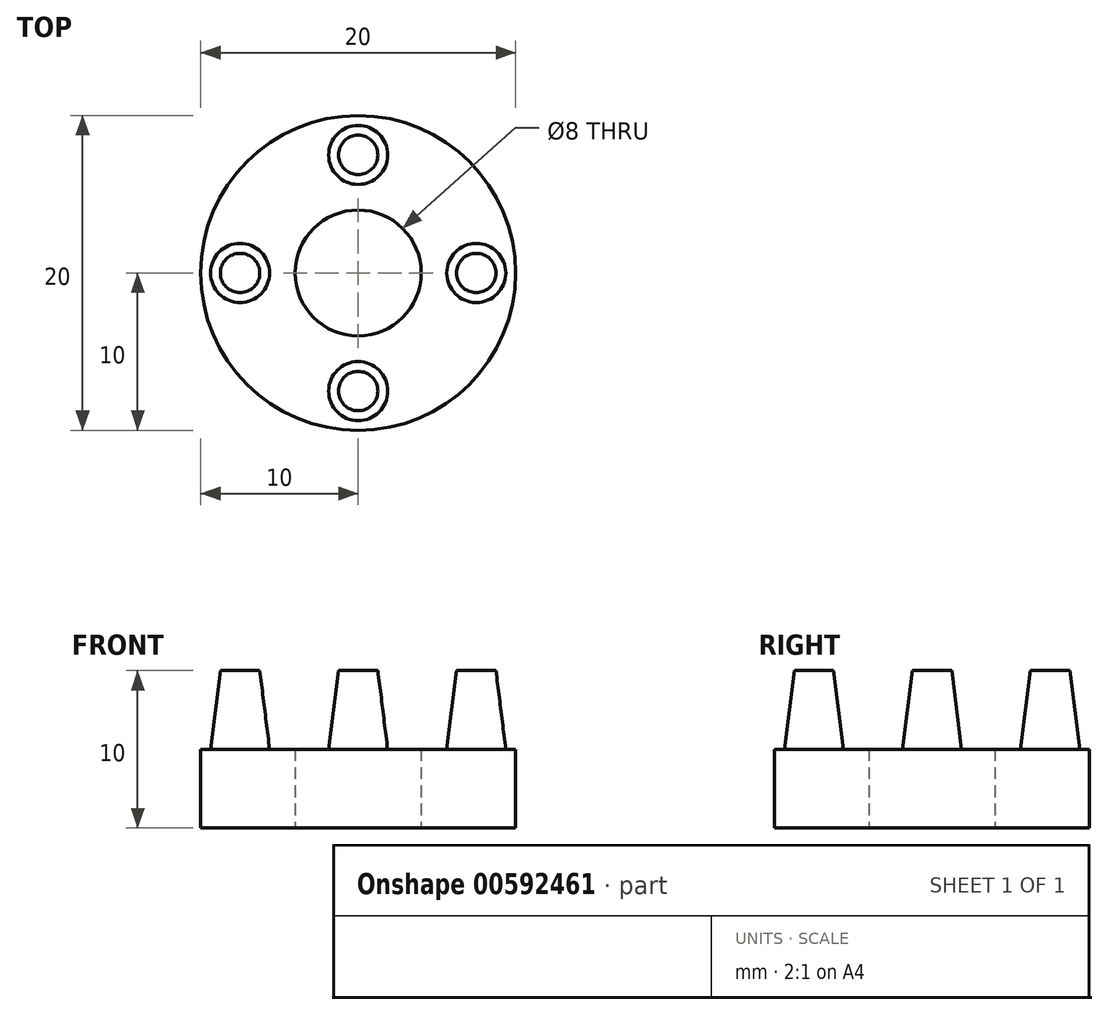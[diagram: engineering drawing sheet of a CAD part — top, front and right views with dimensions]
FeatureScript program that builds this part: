
annotation { "Feature Type Name" : "Feature", "Feature Type Description" : "" }
export const myFeature = defineFeature(function(context is Context, id is Id, definition is map)
    precondition{}
    {
        {
            var Q0;
            Q0=qCreatedBy(makeId("Top.planeOp"),FACE);
            var sketch = newSketch(context, id + "F0", { "sketchPlane" : qUnion([Q0])});
            skCircle(sketch, "E0", {"center": v(0, 0) * mm, "radius": 4 * mm});
            skCircle(sketch, "E1", {"center": v(0, 0) * mm, "radius": 10 * mm});
            skCircle(sketch, "E2", {"center": v(0, 7.5) * mm, "radius": 2.5 * mm});
            skSolve(sketch);
        }
        {
            var Q0;
            {var subQ1=sQuery(id+"F0.wireOp",EDGE,"E2");Q0=makeQuery(id+"F0.imprint","IMPRINT",FACE,{"disambiguationData":[TD([[makeQuery(id+"F0.imprint","IMPRINT",EDGE,{"derivedFrom":subQ1}),-1.0]])]});}
            var Q1;
            Q1=makeQuery(id+"F0.imprint","IMPRINT",FACE,{"disambiguationData":[TD([[makeQuery(id+"F0.imprint","IMPRINT",EDGE,{"derivedFrom":sQuery(id+"F0.wireOp",EDGE,"08f91f88-f108-4c6c-a2ce-b573686cc1aa.1.0")}),1.0]])]});
            var Q2;
            Q2=makeQuery(id+"F0.imprint","IMPRINT",FACE,{"disambiguationData":[TD([[makeQuery(id+"F0.imprint","IMPRINT",EDGE,{"derivedFrom":sQuery(id+"F0.wireOp",EDGE,"08f91f88-f108-4c6c-a2ce-b573686cc1aa.2.0")}),1.0]])]});
            var Q3;
            Q3=makeQuery(id+"F0.imprint","IMPRINT",FACE,{"disambiguationData":[TD([[makeQuery(id+"F0.imprint","IMPRINT",EDGE,{"derivedFrom":sQuery(id+"F0.wireOp",EDGE,"08f91f88-f108-4c6c-a2ce-b573686cc1aa.3.0")}),1.0]])]});
            var Q4;
            Q4=makeQuery(id+"F0.imprint","IMPRINT",FACE,{"disambiguationData":[TD([[makeQuery(id+"F0.imprint","IMPRINT",EDGE,{"derivedFrom":sQuery(id+"F0.wireOp",EDGE,"08f91f88-f108-4c6c-a2ce-b573686cc1aa.4.0")}),1.0]])]});
            var Q5;
            Q5=makeQuery(id+"F0.imprint","IMPRINT",FACE,{"disambiguationData":[TD([[makeQuery(id+"F0.imprint","IMPRINT",EDGE,{"derivedFrom":sQuery(id+"F0.wireOp",EDGE,"E2")}),1.0]])]});
            var Q6;
            Q6=makeQuery(id+"F0.imprint","IMPRINT",FACE,{"disambiguationData":[TD([[makeQuery(id+"F0.imprint","IMPRINT",EDGE,{"derivedFrom":sQuery(id+"F0.wireOp",EDGE,"08f91f88-f108-4c6c-a2ce-b573686cc1aa.5.0")}),1.0]])]});
            var Q7;
            {var subQ0=sQuery(id+"F0.wireOp",EDGE,"xi2heKp6-NqcF-AAX0-xLL8-HdbRwD7PjJWO");Q7=makeQuery(id+"F0.imprint","IMPRINT",FACE,{"disambiguationData":[TD([[makeQuery(id+"F0.imprint","IMPRINT",EDGE,{"derivedFrom":subQ0}),1.0]])]});}
            extrude(context, id + "F1", {"entities" : qUnion([Q0, Q1, Q2, Q3, Q4, Q5, Q6, Q7]), "depth" : 5 * mm, "offsetDistance" : 25 * mm});
        }
        {
            var Q0;
            Q0=makeQuery(id+"F1.opExtrude","CAP_FACE",FACE,{"disambiguationData":[OSD([sQuery(id+"F0.wireOp",EDGE,"E0"),sQuery(id+"F0.wireOp",EDGE,"E1")])],"isStart":false});
            cPlane(context, id + "F2", {"entities" : qUnion([Q0]), "cplaneType" : CPlaneType.OFFSET, "offset" : 5 * mm, "width" : 150 * mm, "height" : 150 * mm});
        }
        {
            var Q0;
            Q0=qCreatedBy(id+"F2.planeOp",FACE);
            var sketch = newSketch(context, id + "F3", { "sketchPlane" : qUnion([Q0])});
            skCircle(sketch, "E3", {"center": v(0, 7.5) * mm, "radius": 1.25 * mm});
            skSolve(sketch);
        }
        {
            var Q1;
            Q1=makeQuery(id+"F3.imprint","IMPRINT",FACE,{"disambiguationData":[TD([[makeQuery(id+"F3.imprint","IMPRINT",EDGE,{"derivedFrom":sQuery(id+"F3.wireOp",EDGE,"E3")}),1.0]])]});
            var Q2;
            Q2=makeQuery(id+"F0.imprint","IMPRINT",FACE,{"disambiguationData":[TD([[makeQuery(id+"F0.imprint","IMPRINT",EDGE,{"derivedFrom":sQuery(id+"F0.wireOp",EDGE,"E2")}),1.0]])]});
            loft(context, id + "F4", {"sheetProfilesArray" : [{ "sheetProfileEntities" : qUnion([Q1]) }, { "sheetProfileEntities" : qUnion([Q2]) }]});
        }
        {
            var Q0;
            Q0=qCreatedBy(makeId("Front.planeOp"),FACE);
            var sketch = newSketch(context, id + "F5", { "sketchPlane" : qUnion([Q0])});
            skLineSegment(sketch, "E4", {"start": v(0, 0) * mm, "end": v(0, 33.97) * mm});
            skSolve(sketch);
        }
        {
            var Q0;
            Q0=makeQuery(id+"F4.opLoft","SWEPT_BODY",BODY,{"disambiguationData":[OSD([makeQuery(id+"F0.imprint","IMPRINT",FACE,{"disambiguationData":[TD([[makeQuery(id+"F0.imprint","IMPRINT",EDGE,{"derivedFrom":sQuery(id+"F0.wireOp",EDGE,"E2")}),1.0]])]}),makeQuery(id+"F3.imprint","IMPRINT",FACE,{"disambiguationData":[TD([[makeQuery(id+"F3.imprint","IMPRINT",EDGE,{"derivedFrom":sQuery(id+"F3.wireOp",EDGE,"E3")}),1.0]])]})])]});
            var Q1;
            Q1=sQuery(id+"F5.wireOp",EDGE,"E4");
            circularPattern(context, id + "F6", {"operationType" : NewBodyOperationType.ADD, "entities" : qUnion([Q0]), "axis" : qUnion([Q1]), "angle" : 360 * degree, "instanceCount" : 4, "equalSpace" : true});
        }
    });
